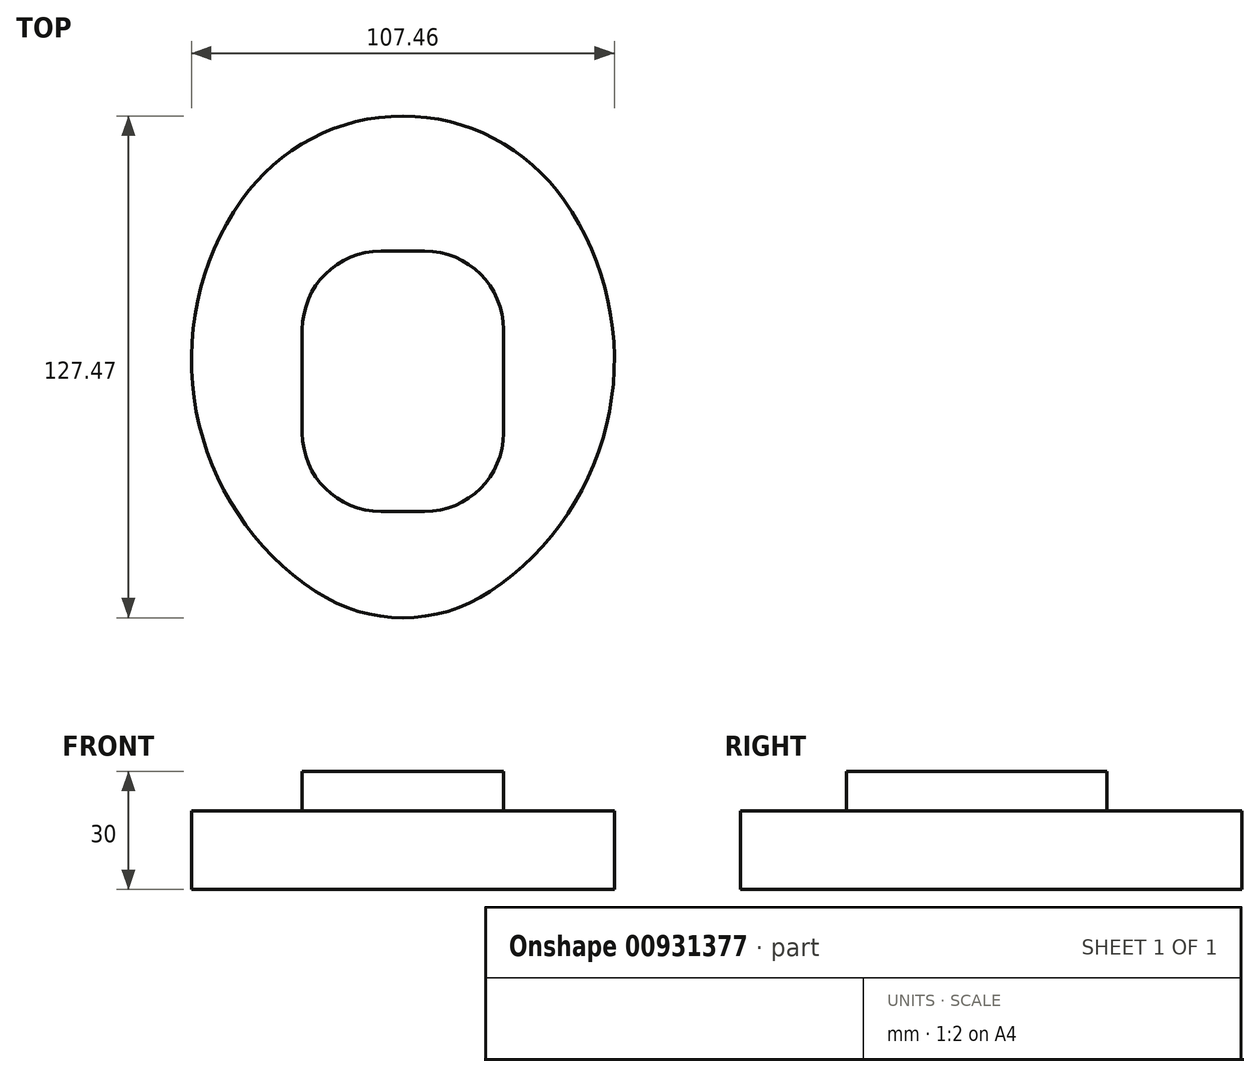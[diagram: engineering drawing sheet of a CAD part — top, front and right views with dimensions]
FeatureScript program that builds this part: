
annotation { "Feature Type Name" : "Feature", "Feature Type Description" : "" }
export const myFeature = defineFeature(function(context is Context, id is Id, definition is map)
    precondition{}
    {
        {
            var Q0;
            Q0=qCreatedBy(makeId("Top.planeOp"),FACE);
            var sketch = newSketch(context, id + "F0", { "sketchPlane" : qUnion([Q0])});
            skArc(sketch, "E0", {"start": v(22.13, -53.4) * mm, "mid": v(52.5, -7.68) * mm, "end": v(41, 46) * mm});
            skArc(sketch, "E1.MirrorCS", {"start": v(-22.13, -53.4) * mm, "mid": v(-52.5, -7.68) * mm, "end": v(-41, 46) * mm});
            skPoint(sketch, "E2.visualSharp", {"position": v(0, 74.17) * mm});
            skArc(sketch, "E2.filletArc", {"start": v(41, 46) * mm, "mid": v(0, 67.38) * mm, "end": v(-41, 46) * mm});
            skPoint(sketch, "E3.visualSharp", {"position": v(0, -63.14) * mm});
            skArc(sketch, "E3.filletArc", {"start": v(-22.13, -53.4) * mm, "mid": v(0, -60.09) * mm, "end": v(22.13, -53.4) * mm});
            skSolve(sketch);
        }
        {
            var Q0;
            Q0=makeQuery(id+"F0.imprint","IMPRINT",FACE,{"disambiguationData":[TD([[makeQuery(id+"F0.imprint","IMPRINT",EDGE,{"derivedFrom":sQuery(id+"F0.wireOp",EDGE,"E0")}),1.0]])]});
            extrude(context, id + "F1", {"entities" : qUnion([Q0]), "depth" : 20 * mm, "offsetDistance" : 25 * mm});
        }
        {
            var Q0;
            Q0=makeQuery(id+"F1.opExtrude","CAP_FACE",FACE,{"disambiguationData":[OSD([sQuery(id+"F0.wireOp",EDGE,"E0"),sQuery(id+"F0.wireOp",EDGE,"E1.MirrorCS"),sQuery(id+"F0.wireOp",EDGE,"E2.filletArc"),sQuery(id+"F0.wireOp",EDGE,"E3.filletArc")])],"isStart":false});
            var sketch = newSketch(context, id + "F2", { "sketchPlane" : qUnion([Q0])});
            skLineSegment(sketch, "E4.bottom", {"start": v(5.55, 33.1) * mm, "end": v(-5.55, 33.1) * mm});
            skLineSegment(sketch, "E4.top", {"start": v(5.55, -33.1) * mm, "end": v(-5.55, -33.1) * mm});
            skLineSegment(sketch, "E4.left", {"start": v(25.55, 13.1) * mm, "end": v(25.55, -13.1) * mm});
            skLineSegment(sketch, "E4.right", {"start": v(-25.55, 13.1) * mm, "end": v(-25.55, -13.1) * mm});
            skPoint(sketch, "E4.middle", {"position": v(0, 0) * mm});
            skPoint(sketch, "E5.visualSharp", {"position": v(-25.55, 33.1) * mm});
            skArc(sketch, "E5.filletArc", {"start": v(-5.55, 33.1) * mm, "mid": v(-19.7, 27.24) * mm, "end": v(-25.55, 13.1) * mm});
            skPoint(sketch, "E6.visualSharp", {"position": v(25.55, 33.1) * mm});
            skArc(sketch, "E6.filletArc", {"start": v(25.55, 13.1) * mm, "mid": v(19.7, 27.24) * mm, "end": v(5.55, 33.1) * mm});
            skPoint(sketch, "E7.visualSharp", {"position": v(25.55, -33.1) * mm});
            skArc(sketch, "E7.filletArc", {"start": v(5.55, -33.1) * mm, "mid": v(19.7, -27.24) * mm, "end": v(25.55, -13.1) * mm});
            skPoint(sketch, "E8.visualSharp", {"position": v(-25.55, -33.1) * mm});
            skArc(sketch, "E8.filletArc", {"start": v(-25.55, -13.1) * mm, "mid": v(-19.7, -27.24) * mm, "end": v(-5.55, -33.1) * mm});
            skSolve(sketch);
        }
        {
            var Q0;
            Q0=makeQuery(id+"F2.imprint","IMPRINT",FACE,{"disambiguationData":[TD([[makeQuery(id+"F2.imprint","IMPRINT",EDGE,{"derivedFrom":sQuery(id+"F2.wireOp",EDGE,"E4.bottom")}),1.0]])]});
            extrude(context, id + "F3", {"entities" : qUnion([Q0]), "operationType" : NewBodyOperationType.ADD, "depth" : 10 * mm, "offsetDistance" : 25 * mm});
        }
    });
